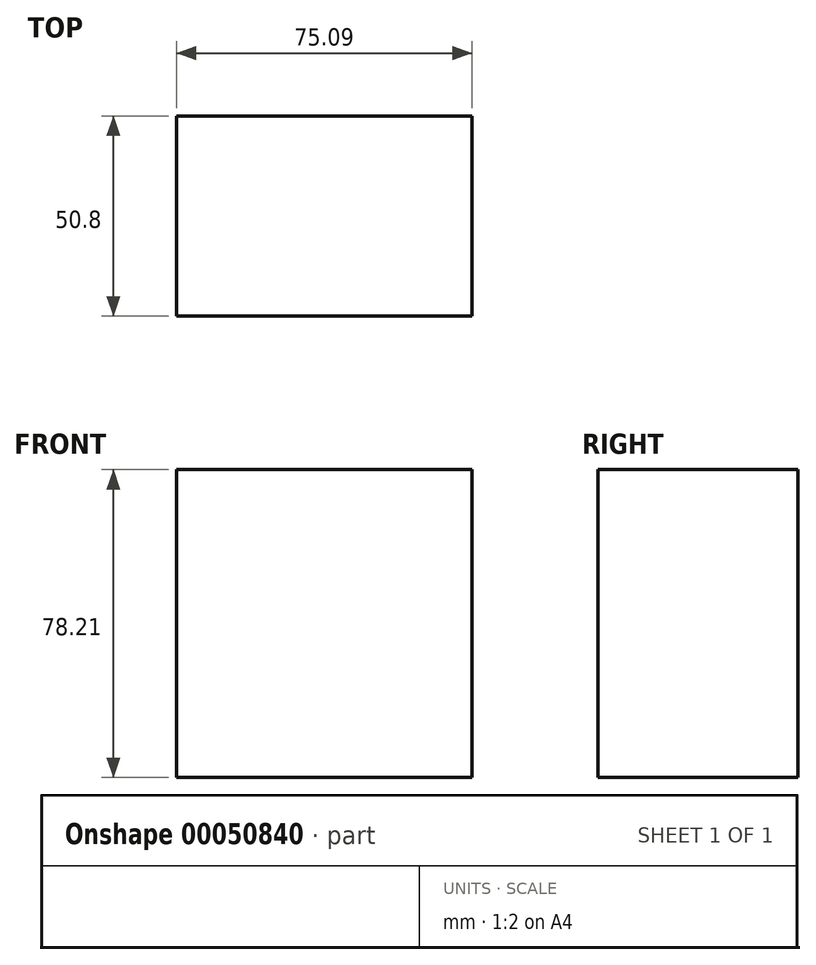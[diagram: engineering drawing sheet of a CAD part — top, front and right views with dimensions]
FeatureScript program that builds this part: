
annotation { "Feature Type Name" : "Feature", "Feature Type Description" : "" }
export const myFeature = defineFeature(function(context is Context, id is Id, definition is map)
    precondition{}
    {
        {
            var Q0;
            Q0=qCreatedBy(makeId("Front.planeOp"),FACE);
            var sketch = newSketch(context, id + "F0", { "sketchPlane" : qUnion([Q0])});
            skLineSegment(sketch, "E0.bottom", {"start": v(0, 0) * mm, "end": v(75.1, 0) * mm});
            skLineSegment(sketch, "E0.top", {"start": v(0, 78.21) * mm, "end": v(75.1, 78.21) * mm});
            skLineSegment(sketch, "E0.left", {"start": v(0, 0) * mm, "end": v(0, 78.21) * mm});
            skLineSegment(sketch, "E0.right", {"start": v(75.1, 0) * mm, "end": v(75.1, 78.21) * mm});
            skSolve(sketch);
        }
        {
            var Q0;
            Q0=makeQuery(id+"F0.imprint","IMPRINT",FACE,{"disambiguationData":[TD([[makeQuery(id+"F0.imprint","IMPRINT",EDGE,{"derivedFrom":sQuery(id+"F0.wireOp",EDGE,"E0.bottom")}),1.0]])]});
            extrude(context, id + "F1", {"entities" : qUnion([Q0]), "depth" : 50.8 * mm});
        }
    });
